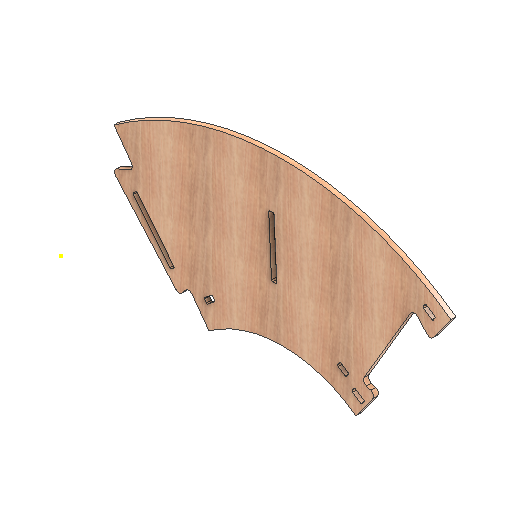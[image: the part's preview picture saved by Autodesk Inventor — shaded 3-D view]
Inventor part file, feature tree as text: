
AUTODESK INVENTOR PART (.ipt)
format: ipt  version: 2021 (Build 250183000, 183)  size: 314,880 bytes
history: native  units: mm
features: other x2, extrude x2, sketch x1, hole x1
ambient origin geometry x8: Origin, YZ Plane, XZ Plane, XY Plane, X Axis, Y Axis, Z Axis, Center Point
bodies: Body1 (feature_tree)
feature tree (6):
  sketch  "Sketch1"  dims[d100=18.0mm d101=0.0mm d102=10.0mm d103=0.0mm]
  other  "CONTOURS"
  hole  "HOLES"  [1 undecoded]
  other  "LETTERS"
  extrude  "Extrusion2"  [1 undecoded]
  extrude  "Extrusion3"  [1 undecoded]
note: 3 required parameter values undecoded (feature->parameter linkage not recoverable at this tier; creation-order binding heuristic only, values carry confidence <= 0.55)
